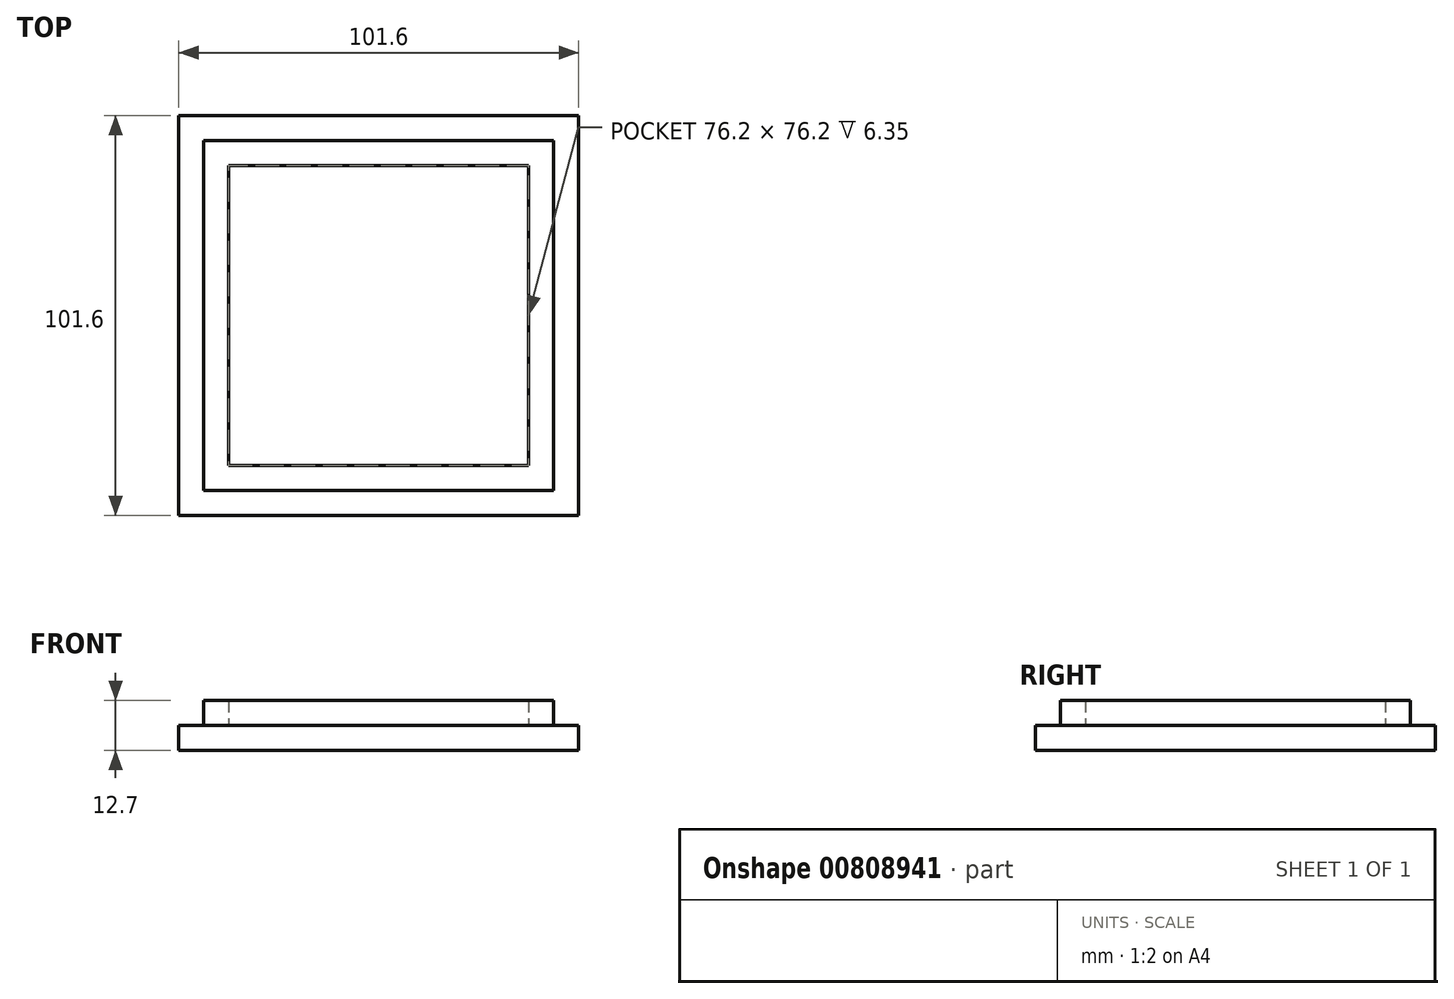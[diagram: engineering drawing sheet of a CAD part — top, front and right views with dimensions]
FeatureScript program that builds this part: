
annotation { "Feature Type Name" : "Feature", "Feature Type Description" : "" }
export const myFeature = defineFeature(function(context is Context, id is Id, definition is map)
    precondition{}
    {
        {
            var Q0;
            Q0=qCreatedBy(makeId("Top.planeOp"),FACE);
            var sketch = newSketch(context, id + "F0", { "sketchPlane" : qUnion([Q0])});
            skLineSegment(sketch, "E0.bottom", {"start": v(50.8, 50.8) * mm, "end": v(-50.8, 50.8) * mm});
            skLineSegment(sketch, "E0.top", {"start": v(50.8, -50.8) * mm, "end": v(-50.8, -50.8) * mm});
            skLineSegment(sketch, "E0.left", {"start": v(50.8, 50.8) * mm, "end": v(50.8, -50.8) * mm});
            skLineSegment(sketch, "E0.right", {"start": v(-50.8, 50.8) * mm, "end": v(-50.8, -50.8) * mm});
            skPoint(sketch, "E0.middle", {"position": v(0, 0) * mm});
            skSolve(sketch);
        }
        {
            var Q0;
            Q0=qSketchRegion(id+"F0",true);
            extrude(context, id + "F1", {"entities" : qUnion([Q0]), "depth" : 6.35 * mm, "offsetDistance" : 25.4 * mm});
        }
        {
            var Q0;
            Q0=makeQuery(id+"F1.opExtrude","CAP_FACE",FACE,{"disambiguationData":[OSD([sQuery(id+"F0.wireOp",EDGE,"E0.bottom"),sQuery(id+"F0.wireOp",EDGE,"E0.top"),sQuery(id+"F0.wireOp",EDGE,"E0.left"),sQuery(id+"F0.wireOp",EDGE,"E0.right")])],"isStart":false});
            var sketch = newSketch(context, id + "F2", { "sketchPlane" : qUnion([Q0])});
            skLineSegment(sketch, "E1.bottom", {"start": v(44.45, 44.45) * mm, "end": v(-44.45, 44.45) * mm});
            skLineSegment(sketch, "E1.top", {"start": v(44.45, -44.45) * mm, "end": v(-44.45, -44.45) * mm});
            skLineSegment(sketch, "E1.left", {"start": v(44.45, 44.45) * mm, "end": v(44.45, -44.45) * mm});
            skLineSegment(sketch, "E1.right", {"start": v(-44.45, 44.45) * mm, "end": v(-44.45, -44.45) * mm});
            skPoint(sketch, "E1.middle", {"position": v(0, 0) * mm});
            skLineSegment(sketch, "E2.bottom", {"start": v(38.1, 38.1) * mm, "end": v(-38.1, 38.1) * mm});
            skLineSegment(sketch, "E2.top", {"start": v(38.1, -38.1) * mm, "end": v(-38.1, -38.1) * mm});
            skLineSegment(sketch, "E2.left", {"start": v(38.1, 38.1) * mm, "end": v(38.1, -38.1) * mm});
            skLineSegment(sketch, "E2.right", {"start": v(-38.1, 38.1) * mm, "end": v(-38.1, -38.1) * mm});
            skSolve(sketch);
        }
        {
            var Q0;
            Q0=makeQuery(id+"F2.imprint","IMPRINT",FACE,{"disambiguationData":[TD([[makeQuery(id+"F2.imprint","IMPRINT",EDGE,{"derivedFrom":sQuery(id+"F2.wireOp",EDGE,"E1.bottom")}),1.0]])]});
            extrude(context, id + "F3", {"entities" : qUnion([Q0]), "operationType" : NewBodyOperationType.ADD, "depth" : 6.35 * mm, "offsetDistance" : 25.4 * mm});
        }
    });
